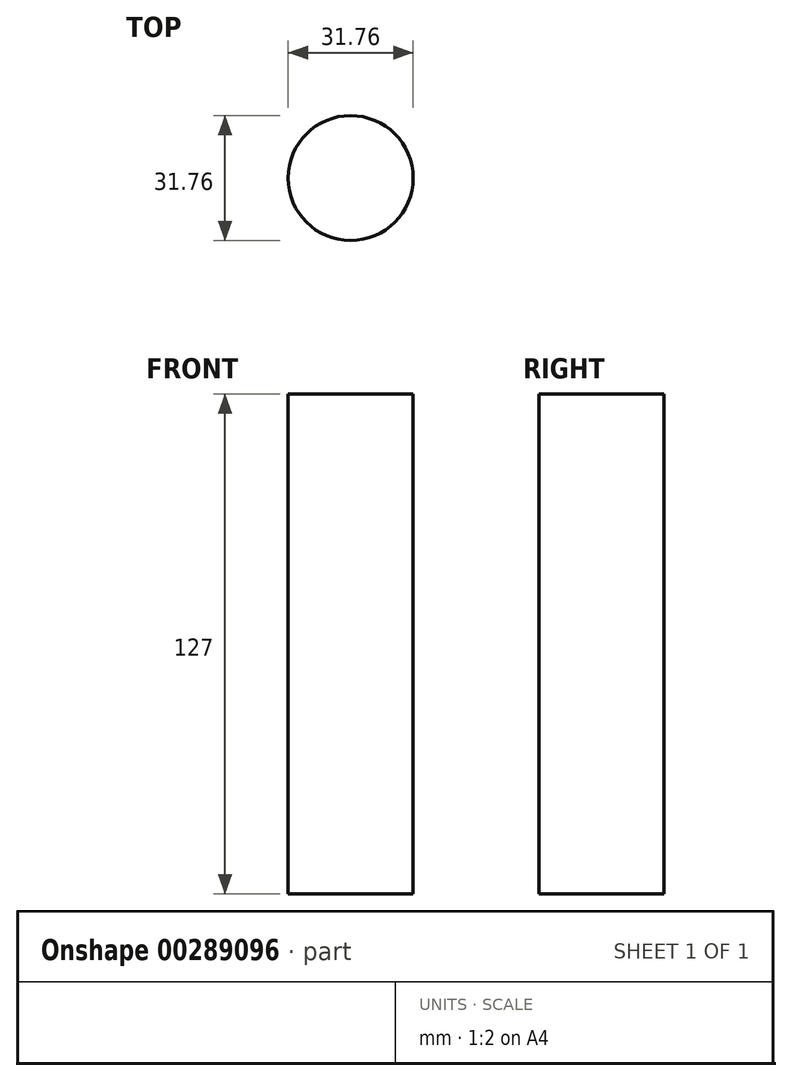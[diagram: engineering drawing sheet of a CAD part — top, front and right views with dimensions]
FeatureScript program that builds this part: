
annotation { "Feature Type Name" : "Feature", "Feature Type Description" : "" }
export const myFeature = defineFeature(function(context is Context, id is Id, definition is map)
    precondition{}
    {
        {
            var Q0;
            Q0=qCreatedBy(makeId("Top.planeOp"),FACE);
            var sketch = newSketch(context, id + "F0", { "sketchPlane" : qUnion([Q0])});
            skCircle(sketch, "E0", {"center": v(0, 0) * mm, "radius": 15.88 * mm});
            skSolve(sketch);
        }
        {
            var Q0;
            Q0=qCreatedBy(makeId("Front.planeOp"),FACE);
            var sketch = newSketch(context, id + "F1", { "sketchPlane" : qUnion([Q0])});
            skLineSegment(sketch, "E1", {"start": v(0, 0) * mm, "end": v(0, 127) * mm});
            skLineSegment(sketch, "E2.0", {"start": v(-15.88, 0) * mm, "end": v(15.88, 0) * mm});
            skFitSpline(sketch, "E3", {"points": [v(-15.88, 0) * mm, v(-20.66, 23.93) * mm, v(-23.58, 43.62) * mm, v(-20.46, 59.8) * mm, v(-29.62, 74.8) * mm, v(-25.14, 89.61) * mm, v(-36.64, 110.86) * mm, v(0, 127) * mm], "startDerivative": vector(-21.17, 202.65) * mm, "endDerivative": vector(342.34, -9.88) * mm});
            skSolve(sketch);
        }
        {
            var Q0;
            Q0=makeQuery(id+"F0.imprint","IMPRINT",FACE,{"disambiguationData":[TD([[makeQuery(id+"F0.imprint","IMPRINT",EDGE,{"derivedFrom":sQuery(id+"F0.wireOp",EDGE,"E0")}),1.0]])]});
            var Q1;
            Q1=sQuery(id+"F1.wireOp",VERTEX,"E1.end");
            extrude(context, id + "F2", {"entities" : qUnion([Q0]), "endBound" : BoundingType.UP_TO_VERTEX, "endBoundEntityVertex" : qUnion([Q1]), "depth" : 25.4 * mm});
        }
        {
            var Q0;
            Q0=qCreatedBy(makeId("Right.planeOp"),FACE);
            var sketch = newSketch(context, id + "F3", { "sketchPlane" : qUnion([Q0])});
            skLineSegment(sketch, "E4.0", {"start": v(-15.88, 0) * mm, "end": v(15.88, 0) * mm});
            skLineSegment(sketch, "E5", {"start": v(-15.88, 0) * mm, "end": v(-15.88, 127) * mm});
            skLineSegment(sketch, "E6.0.0", {"start": v(-15.88, 127) * mm, "end": v(15.88, 127) * mm});
            skSolve(sketch);
        }
        {
            var Q0;
            Q0=sQuery(id+"F1.wireOp",VERTEX,"E3.6.internal");
            var Q1;
            Q1=qCreatedBy(makeId("Top.planeOp"),FACE);
            cPlane(context, id + "F4", {"entities" : qUnion([Q0, Q1]), "cplaneType" : CPlaneType.PLANE_POINT, "offset" : 25.4 * mm, "width" : 152.4 * mm, "height" : 152.4 * mm});
        }
        {
            var Q0;
            Q0=qCreatedBy(id+"F4.planeOp",FACE);
            var sketch = newSketch(context, id + "F5", { "sketchPlane" : qUnion([Q0])});
            skFitSpline(sketch, "E7", {"points": [v(-36.64, 0) * mm, v(0, -15.88) * mm], "startDerivative": vector(-0.83, -26.12) * mm, "endDerivative": vector(34.24, -0.14) * mm});
            skSolve(sketch);
        }
        {
            var Q0;
            Q0 = qSketchRegion(id + "F1", true);
            var Q1;
            Q1=sQuery(id+"F1.wireOp",EDGE,"E3");
            var Q2;
            Q2=sQuery(id+"F3.wireOp",EDGE,"E5");
            var Q3;
            Q3=sQuery(id+"F5.wireOp",EDGE,"E7");
            loft(context, id + "F6", {"bodyType" : ToolBodyType.SURFACE, "addGuides" : true, "sheetProfilesArray" : [{ "sheetProfileEntities" : qUnion([Q0]) }], "wireProfilesArray" : [{ "wireProfileEntities" : qUnion([Q1]) }, { "wireProfileEntities" : qUnion([Q2]) }], "guidesArray" : [{ "guideEntities" : qUnion([Q3]), "guideDerivativeType" : LoftGuideDerivativeType.DEFAULT, "guideDerivativeMagnitude" : 1 }]});
        }
    });
